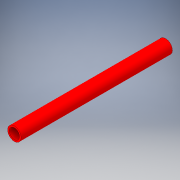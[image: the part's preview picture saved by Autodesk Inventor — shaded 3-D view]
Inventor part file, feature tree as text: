
AUTODESK INVENTOR PART (.ipt)
format: ipt  version: 2018.2 (Build 222227000, 227)  size: 107,520 bytes
history: native  units: in
note: dims shown in document units (in); Inventor stores cm internally (conversion verified against a paired STEP export)
features: extrude x1, sketch x1
ambient origin geometry x8: Origin, YZ Plane, XZ Plane, XY Plane, X Axis, Y Axis, Z Axis, Center Point
bodies: Solid1 (feature_tree)
feature tree (2):
  extrude  "Extrusion1"  Depth=14.698in
  sketch  "Sketch1"  dims[d0=1.315in d1=1.0in d2=14.698in d3=0.0in]
